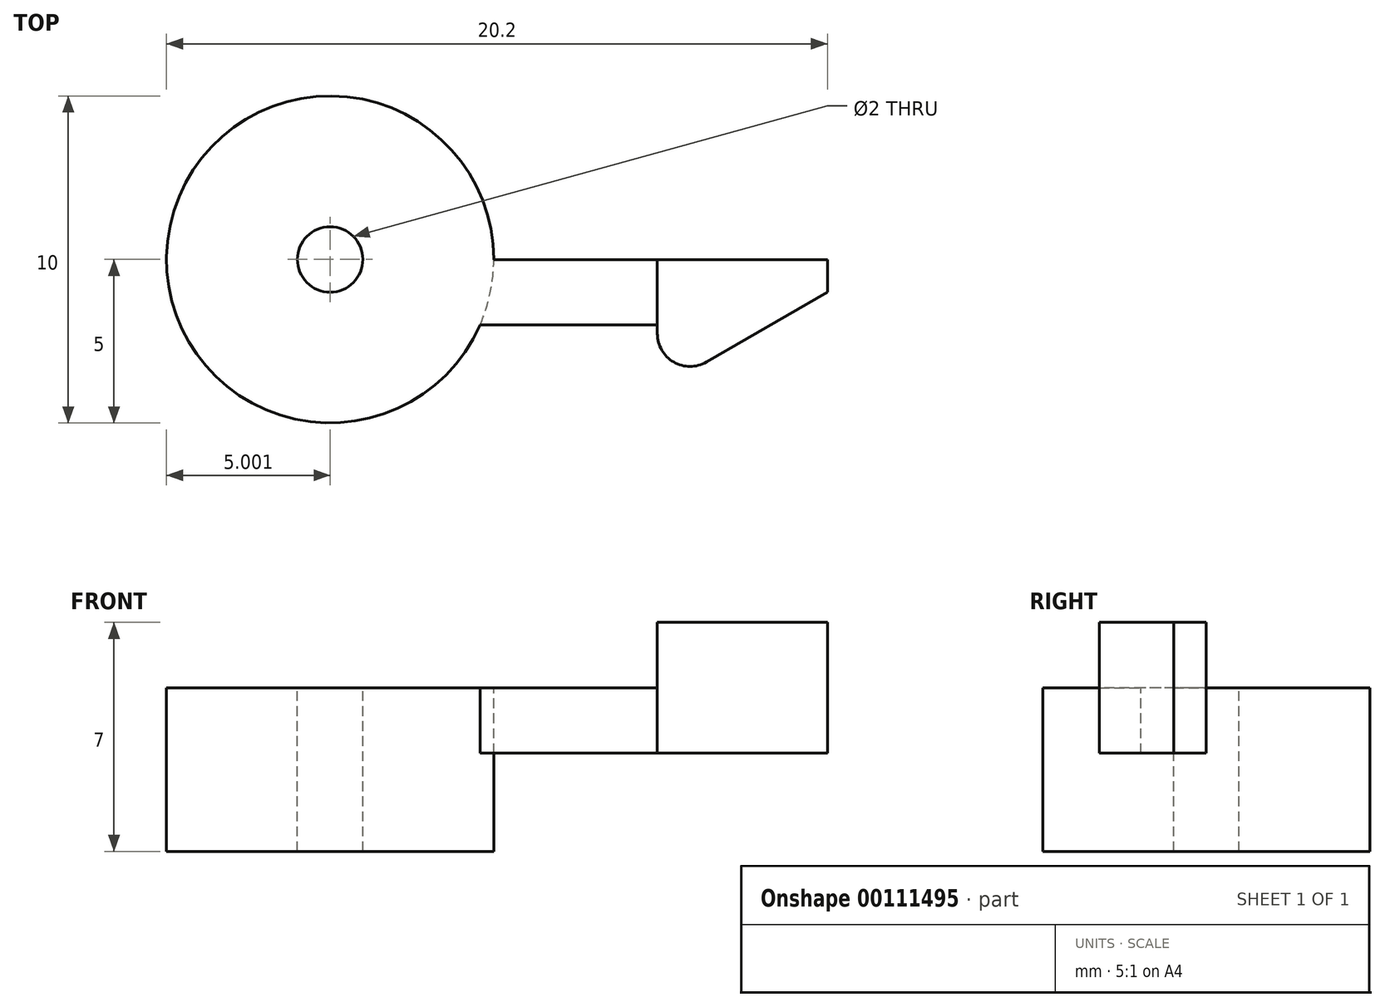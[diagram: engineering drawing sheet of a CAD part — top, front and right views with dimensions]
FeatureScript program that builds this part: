
annotation { "Feature Type Name" : "Feature", "Feature Type Description" : "" }
export const myFeature = defineFeature(function(context is Context, id is Id, definition is map)
    precondition{}
    {
        {
            var Q0;
            Q0=qCreatedBy(makeId("Top.planeOp"),FACE);
            var sketch = newSketch(context, id + "F0", { "sketchPlane" : qUnion([Q0])});
            skCircle(sketch, "E0", {"center": v(-11.14, 0) * mm, "radius": 5 * mm});
            skLineSegment(sketch, "E1", {"start": v(-6.14, 0) * mm, "end": v(-1.14, 0) * mm});
            skLineSegment(sketch, "E2", {"start": v(-1.14, 0) * mm, "end": v(4.06, 0) * mm});
            skLineSegment(sketch, "E3", {"start": v(-1.14, 0) * mm, "end": v(-1.14, -4) * mm});
            skLineSegment(sketch, "E4", {"start": v(4.06, 0) * mm, "end": v(4.06, -1) * mm});
            skLineSegment(sketch, "E5", {"start": v(-1.14, -4) * mm, "end": v(4.06, -1) * mm});
            skLineSegment(sketch, "E6", {"start": v(-1.14, -2) * mm, "end": v(-6.56, -2) * mm});
            skSolve(sketch);
        }
        {
            var Q0;
            {var subQ0=sQuery(id+"F0.wireOp",EDGE,"E0");var subQ1=makeQuery(id+"F0.imprint","INTERSECT",VERTEX,{"derivedFrom":[subQ0,sQuery(id+"F0.wireOp",EDGE,"E1")]});Q0=makeQuery(id+"F0.imprint","IMPRINT",FACE,{"disambiguationData":[TD([[makeQuery(id+"F0.imprint","IMPRINT",EDGE,{"disambiguationData":[TD([[subQ1,1.0]])],"derivedFrom":subQ0}),1.0]])]});}
            extrude(context, id + "F1", {"entities" : qUnion([Q0]), "oppositeDirection" : true, "depth" : 5 * mm});
        }
        {
            var Q0;
            {var subQ0=sQuery(id+"F0.wireOp",EDGE,"E1");Q0=makeQuery(id+"F0.imprint","IMPRINT",FACE,{"disambiguationData":[TD([[makeQuery(id+"F0.imprint","IMPRINT",EDGE,{"derivedFrom":subQ0}),-1.0]])]});}
            extrude(context, id + "F2", {"entities" : qUnion([Q0]), "operationType" : NewBodyOperationType.ADD, "oppositeDirection" : true, "depth" : 2 * mm});
        }
        {
            var Q0;
            {var subQ3=sQuery(id+"F0.wireOp",EDGE,"E2");Q0=makeQuery(id+"F0.imprint","IMPRINT",FACE,{"disambiguationData":[TD([[makeQuery(id+"F0.imprint","IMPRINT",EDGE,{"derivedFrom":subQ3}),-1.0]])]});}
            extrude(context, id + "F3", {"entities" : qUnion([Q0]), "operationType" : NewBodyOperationType.ADD, "endBound" : BoundingType.SYMMETRIC, "depth" : 4 * mm});
        }
        {
            var Q0;
            Q0=makeQuery(id+"F3.opExtrude","SWEPT_EDGE",EDGE,{"disambiguationData":[OSD([sQuery(id+"F0.wireOp",EDGE,"E3"),sQuery(id+"F0.wireOp",EDGE,"E5")])]});
            fillet(context, id + "F4", {"entities" : qUnion([Q0]), "radius" : 1 * mm, "tangentPropagation" : true, "allowEdgeOverflow" : false});
        }
        {
            var Q0;
            Q0=sQuery(id+"F0.wireOp",VERTEX,"E0.center");
            var Q1;
            Q1=makeQuery(id+"F1.opExtrude","SWEPT_BODY",BODY,{"disambiguationData":[OSD([sQuery(id+"F0.wireOp",EDGE,"E0")])]});
            hole(context, id + "F5", {"style" : HoleStyle.SIMPLE, "endStyle" : HoleEndStyle.THROUGH, "holeDiameter" : 2 * mm, "locations" : qUnion([Q0]), "scope" : qUnion([Q1]), "isTappedThrough" : true});
        }
    });
